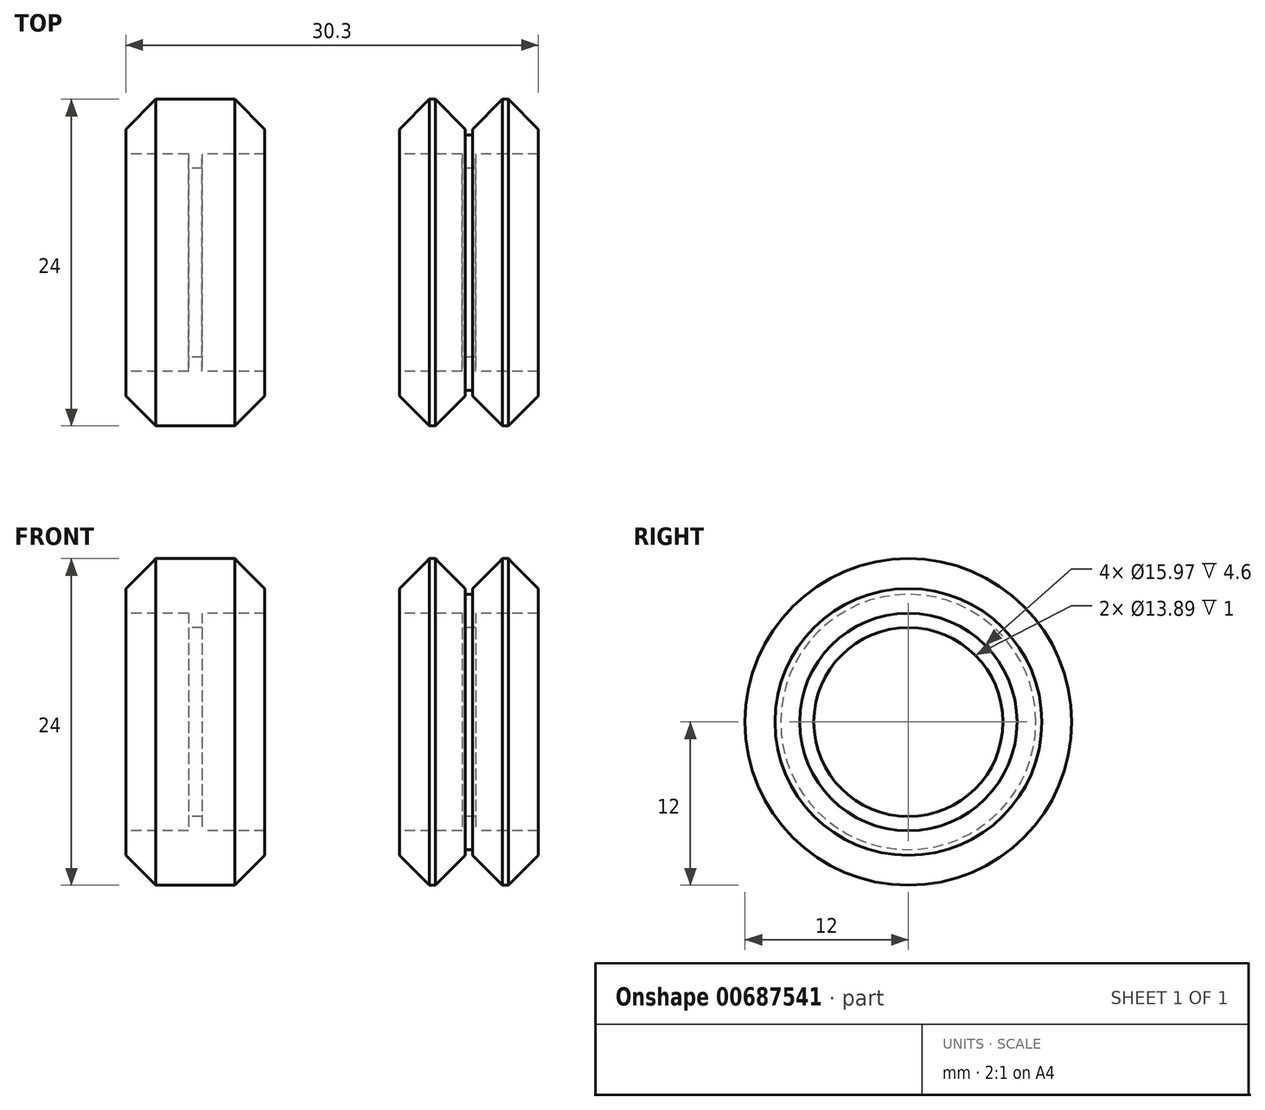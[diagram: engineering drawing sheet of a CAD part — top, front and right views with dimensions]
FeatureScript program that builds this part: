
annotation { "Feature Type Name" : "Feature", "Feature Type Description" : "" }
export const myFeature = defineFeature(function(context is Context, id is Id, definition is map)
    precondition{}
    {
        {
            var Q0;
            Q0=qCreatedBy(makeId("Front.planeOp"),FACE);
            var sketch = newSketch(context, id + "F0", { "sketchPlane" : qUnion([Q0])});
            skLineSegment(sketch, "E0", {"start": v(-5.1, 7.99) * mm, "end": v(-0.5, 7.99) * mm});
            skLineSegment(sketch, "E1", {"start": v(-0.5, 7.99) * mm, "end": v(-0.5, 6.94) * mm});
            skLineSegment(sketch, "E2", {"start": v(-0.5, 6.95) * mm, "end": v(0.5, 6.95) * mm});
            skLineSegment(sketch, "E3", {"start": v(0.5, 6.94) * mm, "end": v(0.5, 7.99) * mm});
            skLineSegment(sketch, "E4", {"start": v(0.5, 7.99) * mm, "end": v(5.1, 7.99) * mm});
            skLineSegment(sketch, "E5", {"start": v(5.1, 7.99) * mm, "end": v(5.1, 9.8) * mm});
            skLineSegment(sketch, "E6", {"start": v(0.28, 9.8) * mm, "end": v(0.28, 9.38) * mm});
            skLineSegment(sketch, "E7", {"start": v(0.28, 9.38) * mm, "end": v(-0.27, 9.38) * mm});
            skLineSegment(sketch, "E8", {"start": v(-0.27, 9.38) * mm, "end": v(-0.27, 9.8) * mm});
            skLineSegment(sketch, "E9", {"start": v(-5.1, 9.8) * mm, "end": v(-5.1, 7.99) * mm});
            skLineSegment(sketch, "E10", {"start": v(0, 6.94) * mm, "end": v(0, 0) * mm, "construction": true});
            skLineSegment(sketch, "E11", {"start": v(0, 0) * mm, "end": v(11.82, 0) * mm, "construction": true});
            skLineSegment(sketch, "E12", {"start": v(-25.2, 7.99) * mm, "end": v(-20.6, 7.99) * mm});
            skLineSegment(sketch, "E13", {"start": v(-20.6, 7.99) * mm, "end": v(-20.6, 6.95) * mm});
            skLineSegment(sketch, "E14", {"start": v(-20.6, 6.95) * mm, "end": v(-19.6, 6.95) * mm});
            skLineSegment(sketch, "E15", {"start": v(-19.6, 6.94) * mm, "end": v(-19.6, 7.99) * mm});
            skLineSegment(sketch, "E16", {"start": v(-19.6, 7.99) * mm, "end": v(-15, 7.99) * mm});
            skLineSegment(sketch, "E17", {"start": v(-15, 7.99) * mm, "end": v(-15, 9.8) * mm});
            skLineSegment(sketch, "E18", {"start": v(-15, 9.8) * mm, "end": v(-17.2, 12) * mm});
            skLineSegment(sketch, "E19", {"start": v(-17.2, 12) * mm, "end": v(-23, 12) * mm});
            skLineSegment(sketch, "E20", {"start": v(-23, 12) * mm, "end": v(-25.2, 9.8) * mm});
            skLineSegment(sketch, "E21", {"start": v(-25.2, 9.8) * mm, "end": v(-25.2, 7.99) * mm});
            skLineSegment(sketch, "E22", {"start": v(-5.1, 9.8) * mm, "end": v(-2.9, 12) * mm});
            skLineSegment(sketch, "E23", {"start": v(-2.9, 12) * mm, "end": v(-2.47, 12) * mm});
            skLineSegment(sketch, "E24", {"start": v(-2.47, 12) * mm, "end": v(-0.27, 9.8) * mm});
            skLineSegment(sketch, "E25", {"start": v(0.28, 9.8) * mm, "end": v(2.47, 12) * mm});
            skLineSegment(sketch, "E26", {"start": v(2.47, 12) * mm, "end": v(2.9, 12) * mm});
            skLineSegment(sketch, "E27", {"start": v(2.9, 12) * mm, "end": v(5.1, 9.8) * mm});
            skSolve(sketch);
        }
        {
            var Q0;
            Q0 = qSketchRegion(id + "F0", true);
            var Q1;
            Q1=sQuery(id+"F0.wireOp",EDGE,"E11");
            revolve(context, id + "F1", {"surfaceOperationType" : NewSurfaceOperationType.NEW, "entities" : qUnion([Q0]), "axis" : qUnion([Q1]), "revolveType" : RevolveType.FULL});
        }
    });
